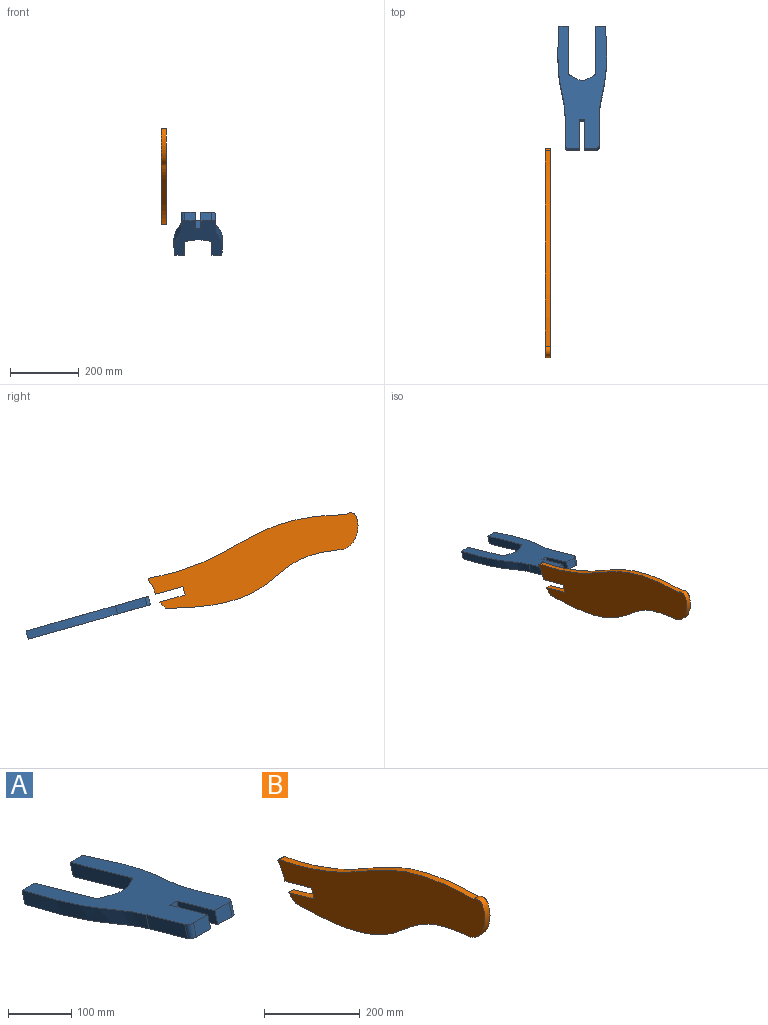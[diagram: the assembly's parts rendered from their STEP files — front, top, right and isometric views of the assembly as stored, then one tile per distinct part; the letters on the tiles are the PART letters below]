
ASSEMBLY  parts=2 mates=1
PART A: 20 faces, bbox 162.4x364.9x125.3 mm
  f0: plane 358.15x162.44mm, normal (0,0.27,0.96), area 30902.6mm2, adj f2,f3,f4,f5,f6,f7,f8,f9
  f1: plane 358.15x162.44mm, normal (0,-0.27,-0.96), area 30902.6mm2, adj f2,f3,f4,f5,f6,f7,f8,f9
  f2: plane 28.17x24.06mm, normal (0,0.96,-0.27), area 704.2mm2, adj f0,f1,f10,f18
  f3: plane 32x24.06mm, normal (0,-0.96,0.27), area 800mm2, adj f0,f1,f7,f12
  f4: plane 28.17x24.06mm, normal (0,0.96,-0.27), area 704.2mm2, adj f0,f1,f14,f19
  f5: plane 32x24.06mm, normal (0,-0.96,0.27), area 800mm2, adj f0,f1,f8,f11
  f6: plane 24.06x16mm, normal (0,-0.96,0.27), area 400mm2, adj f0,f1,f7,f8
  f7: plane 91.71x48.05mm, normal (1,0,0), area 2205.8mm2, adj f0,f1,f3,f6
  f8: plane 91.71x48.05mm, normal (-1,0,0), area 2205.8mm2, adj f0,f1,f5,f6
  f9: plane 93.41x48.53mm, normal (1,0,0), area 2250mm2, adj f0,f1,f10,f11
  f10: extruded ~266.62x97.48mm, area 6793.6mm2, adj f0,f1,f2,f9
  f11: cylinder r=10mm len=26.78mm, axis (0,0.27,0.96), area 392.7mm2, adj f0,f1,f5,f9
  f12: cylinder r=10mm len=26.78mm, axis (0,0.27,0.96), area 392.7mm2, adj f0,f1,f3,f13
  f13: plane 93.41x48.53mm, normal (-1,0,0), area 2250mm2, adj f0,f1,f12,f14
  f14: extruded ~266.62x97.48mm, area 6793.6mm2, adj f0,f1,f4,f13
  f15: cylinder r=10mm len=26.4mm, axis (0,0.27,0.96), area 258.8mm2, adj f0,f1,f16,f19
  f16: extruded ~70.21x28.13mm, area 1929mm2, adj f0,f1,f15,f17
  f17: cylinder r=10mm len=26.4mm, axis (0,0.27,0.96), area 258.8mm2, adj f0,f1,f16,f18
  f18: plane 142.25x62.33mm, normal (-1,0,0), area 3518.8mm2, adj f0,f1,f2,f17
  f19: plane 142.25x62.33mm, normal (1,0,0), area 3518.8mm2, adj f0,f1,f4,f15
PART B: 12 faces, bbox 15x632.2x293 mm
  f0: extruded ~37.99x19.11mm, area 642.4mm2, adj f2,f7,f8,f11
  f1: extruded ~18.53x17.2mm, area 381.7mm2, adj f6,f7,f8,f10
  f2: cylinder r=6mm len=15mm, axis (-1,0,0), area 189.6mm2, adj f0,f3,f7,f8
  f3: extruded ~571.48x184.71mm, area 9113.6mm2, adj f2,f4,f7,f8
  f4: extruded ~108.04x59.89mm, area 2483.3mm2, adj f3,f5,f7,f8
  f5: extruded ~496.56x170.41mm, area 8069.6mm2, adj f4,f6,f7,f8
  f6: cylinder r=6mm len=15mm, axis (-1,0,0), area 51.8mm2, adj f1,f5,f7,f8
  f7: plane 632.18x293.02mm, normal (1,0,0), area 71980.4mm2, adj f0,f1,f2,f3,f4,f5,f6,f9
  f8: plane 632.18x293.02mm, normal (-1,0,0), area 71980.4mm2, adj f0,f1,f2,f3,f4,f5,f6,f9
  f9: plane 24.15x15mm, normal (0,0.96,-0.27), area 376.5mm2, adj f7,f8,f10,f11
  f10: plane 74.6x21.08mm, normal (0,0.27,0.96), area 1162.8mm2, adj f1,f7,f8,f9
  f11: plane 78.89x22.29mm, normal (0,-0.27,-0.96), area 1229.7mm2, adj f0,f7,f8,f9
PLACE A rot(axis=(-0.05,0.1,0.99),0deg) t=(100,185.39,-52.38)mm
PLACE B at identity fixed
MATE slider A.f6 <-> B.f9  axis (0,-0.96,0.27) through (100,306.52,18.8)mm
